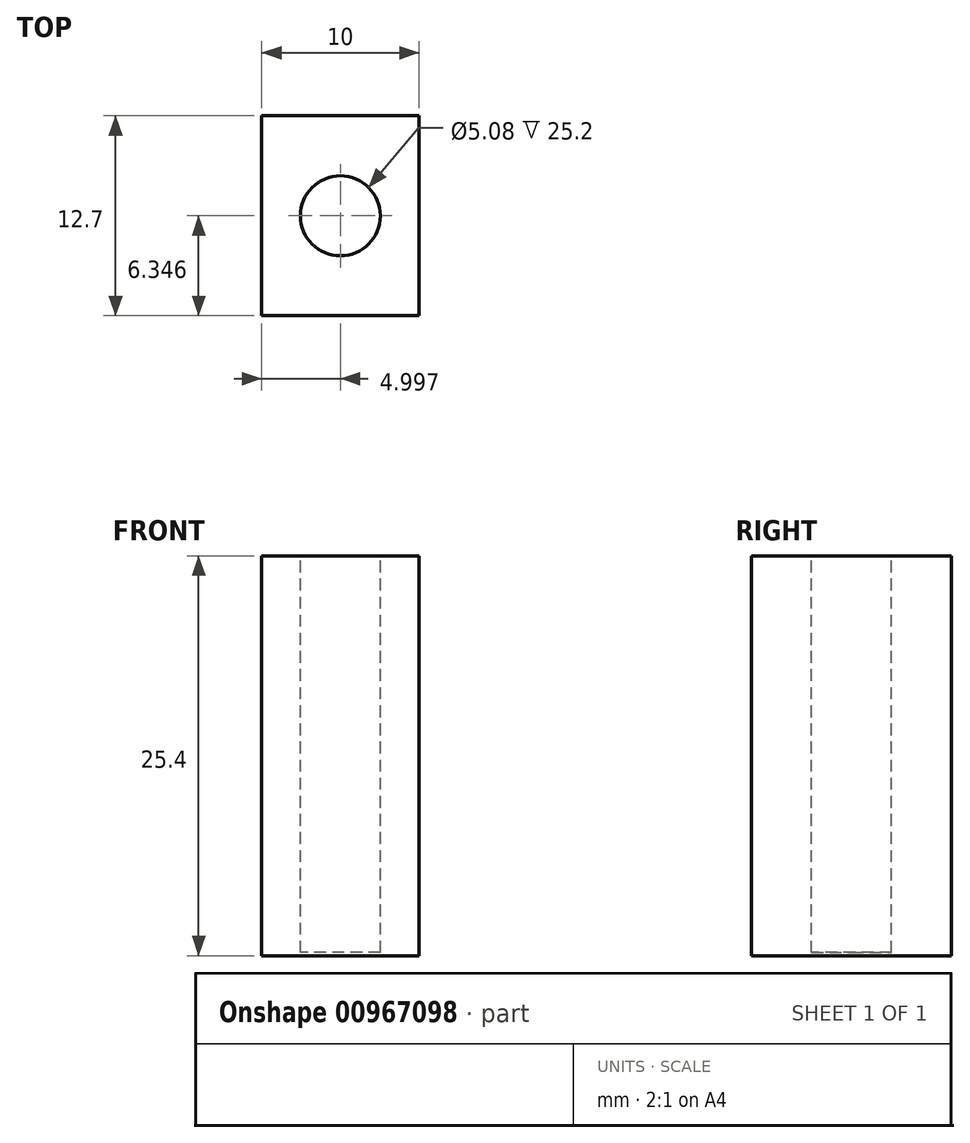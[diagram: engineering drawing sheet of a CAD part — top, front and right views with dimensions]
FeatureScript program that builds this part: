
annotation { "Feature Type Name" : "Feature", "Feature Type Description" : "" }
export const myFeature = defineFeature(function(context is Context, id is Id, definition is map)
    precondition{}
    {
        {
            var Q0;
            Q0=qCreatedBy(makeId("Top.planeOp"),FACE);
            var sketch = newSketch(context, id + "F0", { "sketchPlane" : qUnion([Q0])});
            skLineSegment(sketch, "E0.bottom", {"start": v(-34.23, 55.92) * mm, "end": v(-24.23, 55.92) * mm});
            skLineSegment(sketch, "E0.top", {"start": v(-34.23, 43.22) * mm, "end": v(-24.23, 43.22) * mm});
            skLineSegment(sketch, "E0.left", {"start": v(-34.23, 55.92) * mm, "end": v(-34.23, 43.22) * mm});
            skLineSegment(sketch, "E0.right", {"start": v(-24.23, 55.92) * mm, "end": v(-24.23, 43.22) * mm});
            skSolve(sketch);
        }
        {
            var Q0;
            Q0 = qSketchRegion(id + "F0", true);
            extrude(context, id + "F1", {"entities" : qUnion([Q0]), "endBound" : BoundingType.SYMMETRIC, "depth" : 25.4 * mm, "offsetDistance" : 25.4 * mm});
        }
        {
            var Q0;
            Q0=makeQuery(id+"F1.opExtrude","CAP_FACE",FACE,{"disambiguationData":[OSD([sQuery(id+"F0.wireOp",EDGE,"E0.bottom"),sQuery(id+"F0.wireOp",EDGE,"E0.top"),sQuery(id+"F0.wireOp",EDGE,"E0.left"),sQuery(id+"F0.wireOp",EDGE,"E0.right")])],"isStart":false});
            var sketch = newSketch(context, id + "F2", { "sketchPlane" : qUnion([Q0])});
            skCircle(sketch, "E1", {"center": v(-29.23, 49.57) * mm, "radius": 2.54 * mm});
            skLineSegment(sketch, "E2", {"start": v(-24.23, 49.57) * mm, "end": v(-34.23, 49.57) * mm, "construction": true});
            skSolve(sketch);
        }
        {
            var Q0;
            Q0 = qSketchRegion(id + "F2", true);
            var Q1;
            Q1=makeQuery(id+"F1.opExtrude","CAP_FACE",FACE,{"disambiguationData":[OSD([sQuery(id+"F0.wireOp",EDGE,"E0.bottom"),sQuery(id+"F0.wireOp",EDGE,"E0.top"),sQuery(id+"F0.wireOp",EDGE,"E0.left"),sQuery(id+"F0.wireOp",EDGE,"E0.right")])],"isStart":true});
            extrude(context, id + "F3", {"entities" : qUnion([Q0]), "operationType" : NewBodyOperationType.REMOVE, "endBound" : BoundingType.UP_TO_SURFACE, "oppositeDirection" : true, "depth" : 25.4 * mm, "endBoundEntityFace" : qUnion([Q1]), "hasOffset" : true, "offsetDistance" : .2 * mm});
        }
    });
